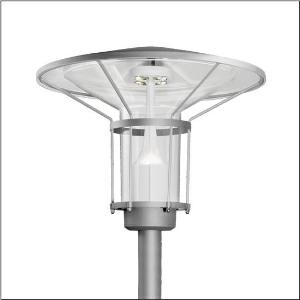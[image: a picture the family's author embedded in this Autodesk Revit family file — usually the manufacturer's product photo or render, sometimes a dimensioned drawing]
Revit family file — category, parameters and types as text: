
# Revit family: laterne_classic_iq___p1_0a_5xa5245nf14h_cdb6
name_source: partatom
category: Lighting Fixtures
units: mm (PartAtom-declared; Revit-internal decimal feet)

## family parameters
Cut with Voids When Loaded = No
Host = Face
Light Source = No
Part Type = Normal
Room Calculation Point = No
Round Connector Dimension = Use Diameter
Shared = No

## types (1)
- --- (1 x LED, 1360 lm, 11.8 W, 2700K)
    Apparent Load = 12 VA
    CIE Flux Codes = 30 61 91 96 100
    Color Rendering = 70
    Color Temperature = 2700K
    Default Elevation = 1800 mm
    Description = Lantern Classic iQ, mast luminaire, Module 540 iQ-SR, primary light control with 3 zone facetted reflector, of plastic, silver coated, highly specular, structured, primary optical cover: cover, of PMMA, transparent, light distribution: P1.0a, light emission: direct distribution, primary light characteristic: strongly asymmetric, installation type: post-top, LED, High Power LED, rated luminous flux: 1.360lm, luminous efficacy: 115lm/W, light colour: 727, colour temperature: 2700K, control gear: ECG iQ, control: presetting dimming logarithmic, Street-Remote, Auto-Match, Temp-Guard, Lumen-Switch, Night-Set, Smart-Wire, Light-Fading, Desk-Remote (wireless, voltage-free reading and setting of iQ features in the workshop via application-optimized NFC function/RFID function), optimised constant luminous flux control (CLO 2.0), with terminal, 6-pole, max. 2.5mm², mains connection: 230..240V, AC, 50/60Hz, start of lifetime: 12W, end of service life: 12W, reduction: 5W, luminaire housing, upper part, of glass-fibre reinforced polyester, coated, Siteco® metallic grey (DB 702S), diameter: 750mm, height: 596mm, spigot size: d x l = 76 x 70mm (post-top) | with reducer (optional accessory) 60 x 70mm, post-top mast mounting element, of diecast aluminium, coated, Siteco® metallic grey (DB 702S), Module 540 iQ-SR, traffic white (RAL 9016), equipment: standard, protection rating (complete): IP65, insulation class (complete): insulation class II (safety insulation), certification: CE, ENEC, VDE, packaging unit: 1 piece

Light Distribution: P1.0a
    Height = 596 mm
    Lamp = 1 x LED
    Lamp Light Flux = 1360 lm
    Lamp Power = 11.8 W
    Lamp count = 1
    Length = 750 mm
    Luminous efficacy = 115 lm/W
    Manufacturer = Siteco
    ModVariant = No
    Model = 5XA5245NF14H
    Number of Poles = 1
    OnlyDefault = Yes
    Power Factor = 1
    Product Name = Laterne Classic iQ | P1.0a
    Product group = mast luminaire | pylon top
    ProductGroupID = 6100
    Protection Class = Protection class II
    Protection Degree = IP 65
    RLX_Detail_Level = 1
    RLX_Emergency_Light_Flux = 0 lm
    RLX_Emergency_Type = 0
    RLX_Emergency_Type_DB = No
    RlxData = <blob elided: 93801 chars, md5=4043829c>
    Socket = socket
    Standby Power = 0 W
    System Light Flux = 1360 lm
    System Power = 12 W
    Type Comments = factory setting: luminous flux: 100 % | dim-lin: 254 | 472 mA
    Type Image = l_1006052.jpg
    URL = http://relux.com
    VarID = @adj_085615
    Voltage = 0 V
    Weight = 0.00 kg
    Width = 0 mm  [stored 0 ft]

note: [stored X ft] marks values corroborated as IEEE doubles in the binary element streams (Revit-internal decimal feet)

## geometry (parser evidence)
native form markers: Blend x4, Sweep x11
no freeform markers — native parametric forms only
